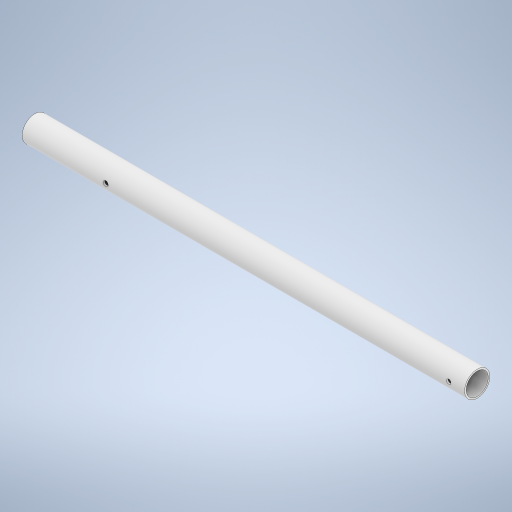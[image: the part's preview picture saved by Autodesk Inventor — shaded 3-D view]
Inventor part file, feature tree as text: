
AUTODESK INVENTOR PART (.ipt)
format: ipt  version: 2023 (Build 270158030, 158C)  size: 262,144 bytes
history: native  units: in
note: dims shown in document units (in); Inventor stores cm internally (conversion verified against a paired STEP export)
features: extrude x3, sketch x3
ambient origin geometry x8: Origin, YZ Plane, XZ Plane, XY Plane, X Axis, Y Axis, Z Axis, Center Point
bodies: Solid1 (feature_tree)
feature tree (6):
  extrude  "Extrusion1"  Depth=0.154in
  extrude  "Extrusion3"  Depth=0.4134in
  extrude  "Extrusion5"  TaperAngle=0.0deg  [1 undecoded]
  sketch  "Sketch1"  dims[d0=2.067in d1=0.154in]
  sketch  "Sketch3"  dims[d2=41.7323in d3=0.0in d8=0.4134in]
  sketch  "Sketch5"  dims[d9=1.5in d10=0.0in d11=0.0in d17=0.4724in d18=7.874in d19=0.0in d20=0.0in]
note: 1 required parameter value undecoded (feature->parameter linkage not recoverable at this tier; creation-order binding heuristic only, values carry confidence <= 0.55)
